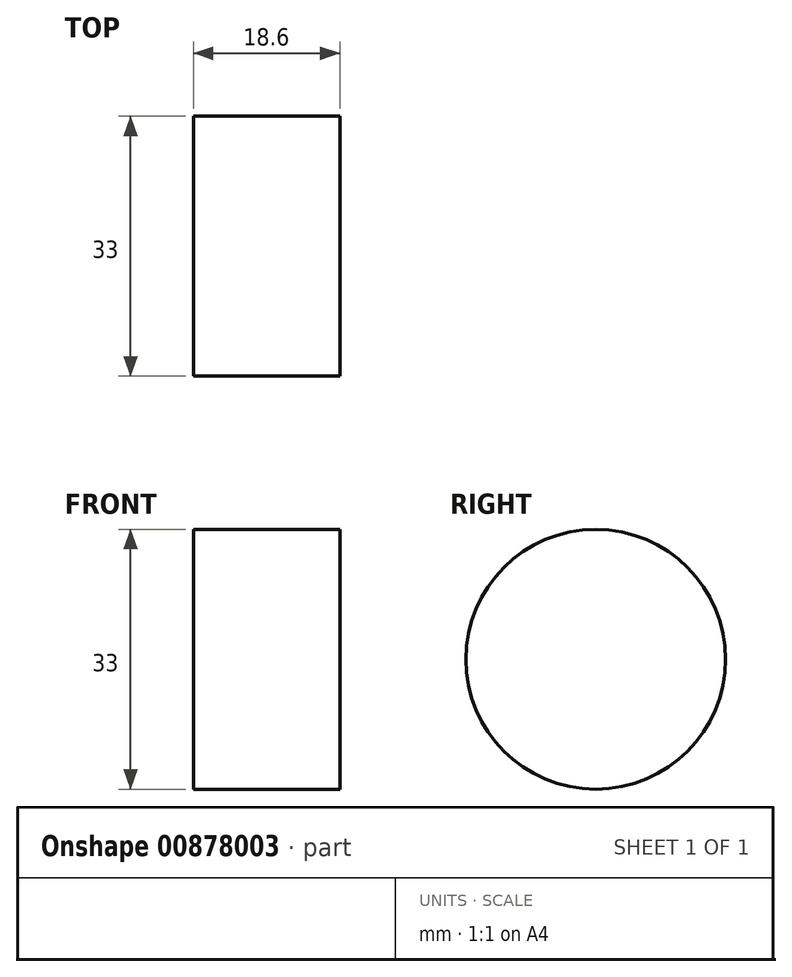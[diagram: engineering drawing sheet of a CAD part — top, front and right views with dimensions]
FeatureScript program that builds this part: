
annotation { "Feature Type Name" : "Feature", "Feature Type Description" : "" }
export const myFeature = defineFeature(function(context is Context, id is Id, definition is map)
    precondition{}
    {
        {
            var Q0;
            Q0=qCreatedBy(makeId("Right.planeOp"),FACE);
            var sketch = newSketch(context, id + "F0", { "sketchPlane" : qUnion([Q0])});
            skCircle(sketch, "E0", {"center": v(0, 0) * mm, "radius": 16.5 * mm});
            skSolve(sketch);
        }
        {
            var Q0;
            Q0=makeQuery(id+"F0.imprint","IMPRINT",FACE,{"disambiguationData":[TD([[makeQuery(id+"F0.imprint","IMPRINT",EDGE,{"derivedFrom":sQuery(id+"F0.wireOp",EDGE,"E0")}),1.0]])]});
            extrude(context, id + "F1", {"entities" : qUnion([Q0]), "depth" : 18.6 * mm});
        }
    });
